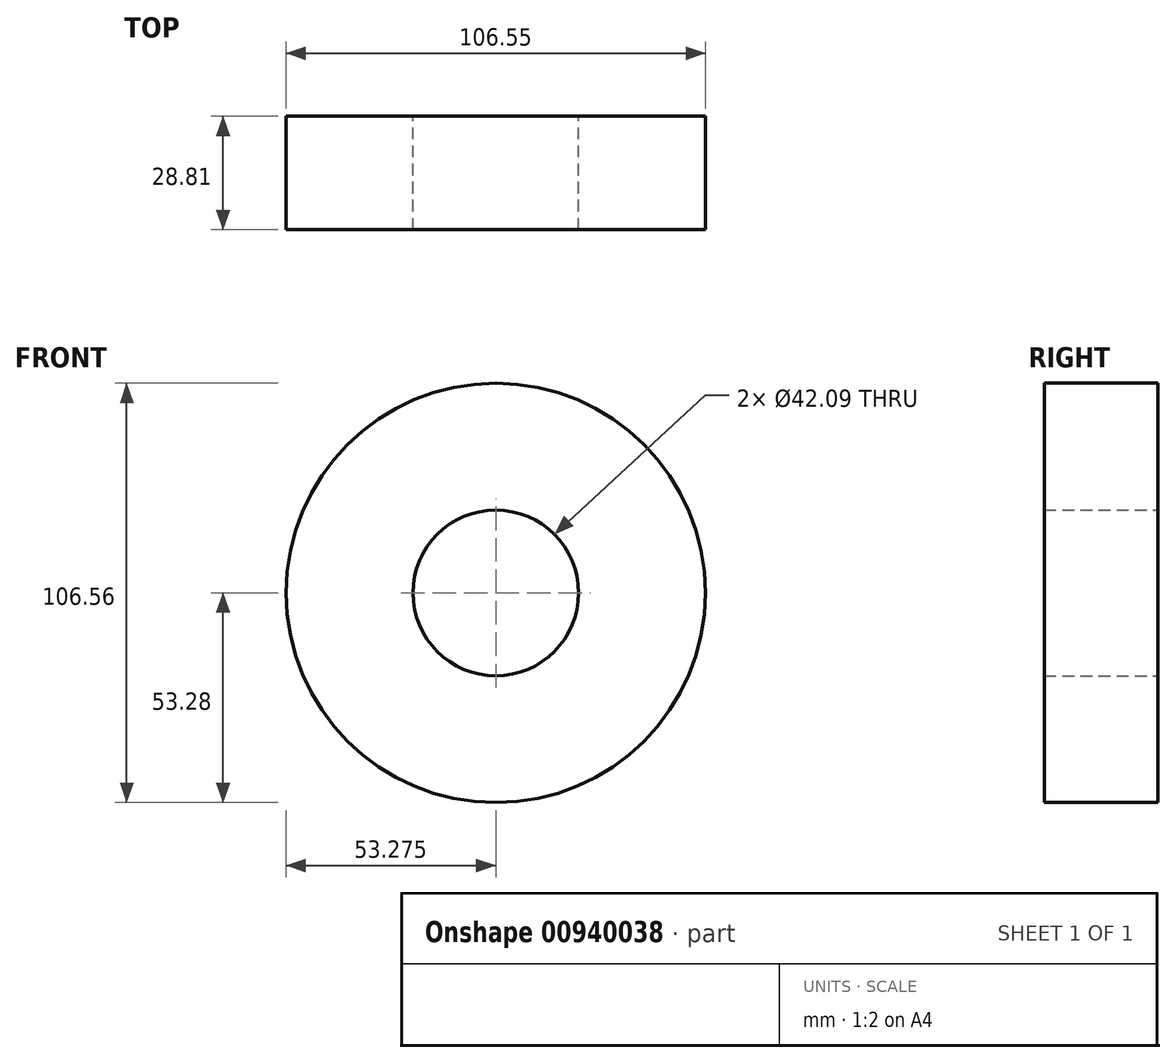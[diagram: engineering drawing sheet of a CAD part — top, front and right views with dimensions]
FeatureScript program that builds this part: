
annotation { "Feature Type Name" : "Feature", "Feature Type Description" : "" }
export const myFeature = defineFeature(function(context is Context, id is Id, definition is map)
    precondition{}
    {
        {
            var Q0;
            Q0=qCreatedBy(makeId("Top.planeOp"),FACE);
            var sketch = newSketch(context, id + "F0", { "sketchPlane" : qUnion([Q0])});
            skLineSegment(sketch, "E0.bottom", {"start": v(-58.11, 33.46) * mm, "end": v(-25.88, 33.46) * mm});
            skLineSegment(sketch, "E0.top", {"start": v(-58.11, 4.65) * mm, "end": v(-25.88, 4.65) * mm});
            skLineSegment(sketch, "E0.left", {"start": v(-58.11, 33.46) * mm, "end": v(-58.11, 4.65) * mm});
            skLineSegment(sketch, "E0.right", {"start": v(-25.88, 33.46) * mm, "end": v(-25.88, 4.65) * mm});
            skLineSegment(sketch, "E1", {"start": v(-4.83, 38.01) * mm, "end": v(-4.83, 2.37) * mm});
            skSolve(sketch);
        }
        {
            var Q0;
            Q0=makeQuery(id+"F0.imprint","IMPRINT",FACE,{"disambiguationData":[TD([[makeQuery(id+"F0.imprint","IMPRINT",EDGE,{"derivedFrom":sQuery(id+"F0.wireOp",EDGE,"E0.bottom")}),-1.0]])]});
            var Q1;
            Q1=sQuery(id+"F0.wireOp",EDGE,"E1");
            revolve(context, id + "F1", {"surfaceOperationType" : NewSurfaceOperationType.NEW, "entities" : qUnion([Q0]), "axis" : qUnion([Q1]), "revolveType" : RevolveType.FULL});
        }
    });
